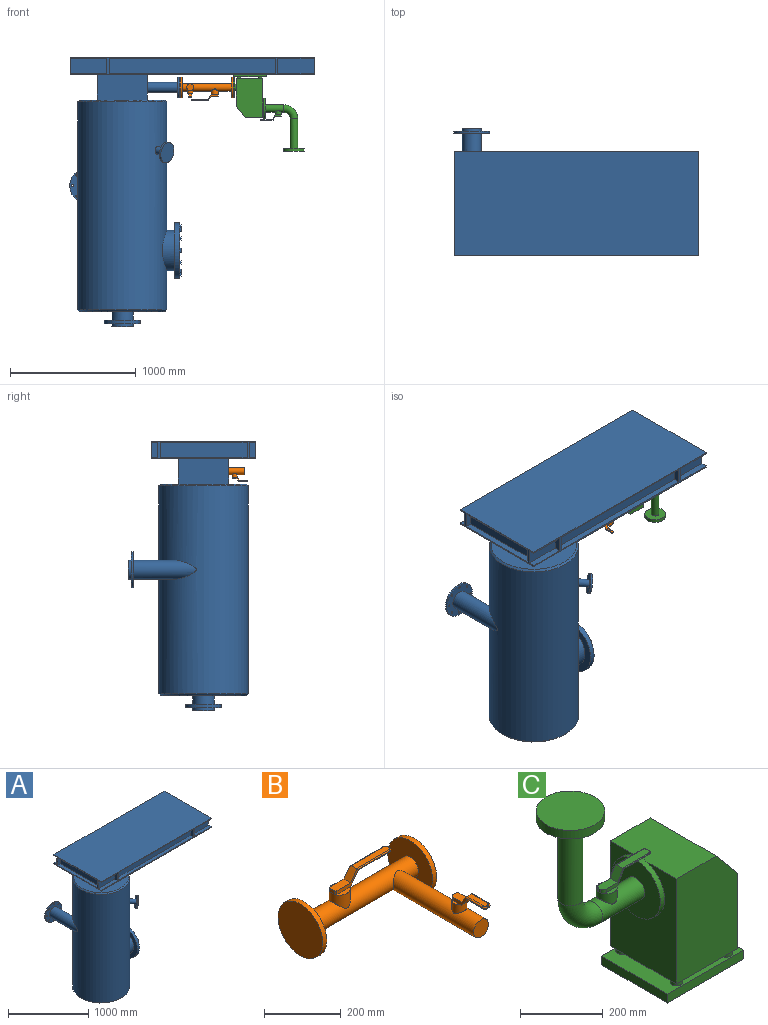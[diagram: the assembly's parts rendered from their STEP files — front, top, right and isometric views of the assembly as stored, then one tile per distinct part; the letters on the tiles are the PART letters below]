
ASSEMBLY  parts=3 mates=3
PART A: 183 faces, bbox 1942.5x1015x2142 mm
  f0: plane 830x140mm, normal (-1,0,0), area 21400mm2, adj f2,f3,f129,f130,f144,f146,f147,f153
  f1: plane 830x140mm, normal (1,0,0), area 21400mm2, adj f2,f3,f129,f130,f140,f141,f143,f157
  f2: plane 1940x140mm, normal (0,-1,0), area 43600mm2, adj f0,f1,f129,f130,f148,f149,f150,f151
  f3: plane 1940x140mm, normal (0,1,0), area 43600mm2, adj f0,f1,f129,f130,f135,f136,f137,f138
  f4: cylinder r=355mm len=1652mm, axis (0,0,-1), area 3567773.8mm2, adj f7,f10,f24,f111,f131
  f5: cylinder r=85mm len=170mm, axis (0,0,1), area 37385mm2, adj f9,f113
  f6: plane 445x445mm, normal (1,0,0), area 146689.4mm2, adj f25,f27,f28,f29,f30,f31,f32,f34
  f7: cylinder r=75mm len=500.65mm, axis (0,-1,0), area 167787.6mm2, adj f4,f13
  f8: plane 680x680mm, normal (0,0,1), area 203168.1mm2, adj f10,f125,f126,f127,f128
  f9: plane 680x680mm, normal (0,0,-1), area 340470.1mm2, adj f5,f111
  f10: cone r=355mm half-angle=45deg, axis (0,0,-1), area 46317.1mm2, adj f4,f8
  f11: cylinder r=142.5mm len=285mm, axis (0,-1,0), area 13430.3mm2, adj f12,f13
  f12: plane 285x285mm, normal (0,1,0), area 44086.8mm2, adj f11,f15,f16,f17,f18,f19,f20,f21
  f13: plane 285x285mm, normal (0,-1,0), area 44086.8mm2, adj f7,f11,f16,f17,f18,f19,f20,f21
  f14: plane 150x150mm, normal (0,1,0), area 17671.5mm2, adj f15
  f15: cylinder r=75mm len=150mm, axis (0,-1,0), area 11781mm2, adj f12,f14
  f16: cylinder r=9mm len=18mm, axis (0,1,0), area 848.2mm2, adj f12,f13
  f17: cylinder r=9mm len=18mm, axis (0,1,0), area 848.2mm2, adj f12,f13
  f18: cylinder r=9mm len=18mm, axis (0,1,0), area 848.2mm2, adj f12,f13
  f19: cylinder r=9mm len=18mm, axis (0,1,0), area 848.2mm2, adj f12,f13
  f20: cylinder r=9mm len=18mm, axis (0,1,0), area 848.2mm2, adj f12,f13
  f21: cylinder r=9mm len=18mm, axis (0,1,0), area 848.2mm2, adj f12,f13
  f22: cylinder r=9mm len=18mm, axis (0,1,0), area 848.2mm2, adj f12,f13
  f23: cylinder r=9mm len=18mm, axis (0,1,0), area 848.2mm2, adj f12,f13
  f24: cylinder r=160mm len=320mm, axis (-1,0,0), area 79181.6mm2, adj f4,f26
  f25: cylinder r=222.5mm len=445mm, axis (-1,0,0), area 55920.3mm2, adj f6,f26
  f26: plane 445x445mm, normal (-1,0,0), area 75103.7mm2, adj f24,f25
  f27: plane 15x14.58mm, normal (0,-0.87,0.5), area 252.6mm2, adj f6,f28,f32,f33
  f28: plane 15x14.58mm, normal (0,-0.87,-0.5), area 252.6mm2, adj f6,f27,f29,f33
  f29: plane 16.84x15mm, normal (0,0,-1), area 252.6mm2, adj f6,f28,f30,f33
  f30: plane 15x14.58mm, normal (0,0.87,-0.5), area 252.6mm2, adj f6,f29,f31,f33
  f31: plane 15x14.58mm, normal (0,0.87,0.5), area 252.6mm2, adj f6,f30,f32,f33
  f32: plane 16.84x15mm, normal (0,0,1), area 252.6mm2, adj f6,f27,f31,f33
  f33: plane 33.68x29.16mm, normal (1,0,0), area 736.6mm2, adj f27,f28,f29,f30,f31,f32
  f34: plane 15x14.58mm, normal (0,-0.5,-0.87), area 252.6mm2, adj f6,f35,f39,f40
  f35: plane 15x14.58mm, normal (0,0.5,-0.87), area 252.6mm2, adj f6,f34,f36,f40
  f36: plane 16.84x15mm, normal (0,1,0), area 252.6mm2, adj f6,f35,f37,f40
  f37: plane 15x14.58mm, normal (0,0.5,0.87), area 252.6mm2, adj f6,f36,f38,f40
  f38: plane 15x14.58mm, normal (0,-0.5,0.87), area 252.6mm2, adj f6,f37,f39,f40
  f39: plane 16.84x15mm, normal (0,-1,0), area 252.6mm2, adj f6,f34,f38,f40
  f40: plane 33.68x29.16mm, normal (1,0,0), area 736.6mm2, adj f34,f35,f36,f37,f38,f39
  f41: plane 16.84x15mm, normal (0,0,-1), area 252.6mm2, adj f6,f42,f46,f47
  f42: plane 15x14.58mm, normal (0,0.87,-0.5), area 252.6mm2, adj f6,f41,f43,f47
  f43: plane 15x14.58mm, normal (0,0.87,0.5), area 252.6mm2, adj f6,f42,f44,f47
  f44: plane 16.84x15mm, normal (0,0,1), area 252.6mm2, adj f6,f43,f45,f47
  f45: plane 15x14.58mm, normal (0,-0.87,0.5), area 252.6mm2, adj f6,f44,f46,f47
  f46: plane 15x14.58mm, normal (0,-0.87,-0.5), area 252.6mm2, adj f6,f41,f45,f47
  f47: plane 33.68x29.16mm, normal (1,0,0), area 736.6mm2, adj f41,f42,f43,f44,f45,f46
  f48: plane 15x14.58mm, normal (0,0.5,-0.87), area 252.6mm2, adj f6,f49,f53,f54
  f49: plane 16.84x15mm, normal (0,1,0), area 252.6mm2, adj f6,f48,f50,f54
  f50: plane 15x14.58mm, normal (0,0.5,0.87), area 252.6mm2, adj f6,f49,f51,f54
  f51: plane 15x14.58mm, normal (0,-0.5,0.87), area 252.6mm2, adj f6,f50,f52,f54
  f52: plane 16.84x15mm, normal (0,-1,0), area 252.6mm2, adj f6,f51,f53,f54
  f53: plane 15x14.58mm, normal (0,-0.5,-0.87), area 252.6mm2, adj f6,f48,f52,f54
  f54: plane 33.68x29.16mm, normal (1,0,0), area 736.6mm2, adj f48,f49,f50,f51,f52,f53
  f55: plane 15x14.58mm, normal (0,0.87,-0.5), area 252.6mm2, adj f6,f56,f60,f61
  f56: plane 15x14.58mm, normal (0,0.87,0.5), area 252.6mm2, adj f6,f55,f57,f61
  f57: plane 16.84x15mm, normal (0,0,1), area 252.6mm2, adj f6,f56,f58,f61
  f58: plane 15x14.58mm, normal (0,-0.87,0.5), area 252.6mm2, adj f6,f57,f59,f61
  f59: plane 15x14.58mm, normal (0,-0.87,-0.5), area 252.6mm2, adj f6,f58,f60,f61
  f60: plane 16.84x15mm, normal (0,0,-1), area 252.6mm2, adj f6,f55,f59,f61
  f61: plane 33.68x29.16mm, normal (1,0,0), area 736.6mm2, adj f55,f56,f57,f58,f59,f60
  f62: plane 16.84x15mm, normal (0,1,0), area 252.6mm2, adj f6,f63,f67,f68
  f63: plane 15x14.58mm, normal (0,0.5,0.87), area 252.6mm2, adj f6,f62,f64,f68
  f64: plane 15x14.58mm, normal (0,-0.5,0.87), area 252.6mm2, adj f6,f63,f65,f68
  f65: plane 16.84x15mm, normal (0,-1,0), area 252.6mm2, adj f6,f64,f66,f68
  f66: plane 15x14.58mm, normal (0,-0.5,-0.87), area 252.6mm2, adj f6,f65,f67,f68
  f67: plane 15x14.58mm, normal (0,0.5,-0.87), area 252.6mm2, adj f6,f62,f66,f68
  f68: plane 33.68x29.16mm, normal (1,0,0), area 736.6mm2, adj f62,f63,f64,f65,f66,f67
  f69: plane 15x14.58mm, normal (0,0.87,0.5), area 252.6mm2, adj f6,f70,f74,f75
  f70: plane 16.84x15mm, normal (0,0,1), area 252.6mm2, adj f6,f69,f71,f75
  f71: plane 15x14.58mm, normal (0,-0.87,0.5), area 252.6mm2, adj f6,f70,f72,f75
  f72: plane 15x14.58mm, normal (0,-0.87,-0.5), area 252.6mm2, adj f6,f71,f73,f75
  f73: plane 16.84x15mm, normal (0,0,-1), area 252.6mm2, adj f6,f72,f74,f75
  f74: plane 15x14.58mm, normal (0,0.87,-0.5), area 252.6mm2, adj f6,f69,f73,f75
  f75: plane 33.68x29.16mm, normal (1,0,0), area 736.6mm2, adj f69,f70,f71,f72,f73,f74
  f76: plane 15x14.58mm, normal (0,0.5,0.87), area 252.6mm2, adj f6,f77,f81,f82
  f77: plane 15x14.58mm, normal (0,-0.5,0.87), area 252.6mm2, adj f6,f76,f78,f82
  f78: plane 16.84x15mm, normal (0,-1,0), area 252.6mm2, adj f6,f77,f79,f82
  f79: plane 15x14.58mm, normal (0,-0.5,-0.87), area 252.6mm2, adj f6,f78,f80,f82
  f80: plane 15x14.58mm, normal (0,0.5,-0.87), area 252.6mm2, adj f6,f79,f81,f82
  f81: plane 16.84x15mm, normal (0,1,0), area 252.6mm2, adj f6,f76,f80,f82
  f82: plane 33.68x29.16mm, normal (1,0,0), area 736.6mm2, adj f76,f77,f78,f79,f80,f81
  f83: plane 16.84x15mm, normal (0,0,1), area 252.6mm2, adj f6,f84,f88,f89
  f84: plane 15x14.58mm, normal (0,-0.87,0.5), area 252.6mm2, adj f6,f83,f85,f89
  f85: plane 15x14.58mm, normal (0,-0.87,-0.5), area 252.6mm2, adj f6,f84,f86,f89
  f86: plane 16.84x15mm, normal (0,0,-1), area 252.6mm2, adj f6,f85,f87,f89
  f87: plane 15x14.58mm, normal (0,0.87,-0.5), area 252.6mm2, adj f6,f86,f88,f89
  f88: plane 15x14.58mm, normal (0,0.87,0.5), area 252.6mm2, adj f6,f83,f87,f89
  f89: plane 33.68x29.16mm, normal (1,0,0), area 736.6mm2, adj f83,f84,f85,f86,f87,f88
  f90: plane 15x14.58mm, normal (0,-0.5,0.87), area 252.6mm2, adj f6,f91,f95,f96
  f91: plane 16.84x15mm, normal (0,-1,0), area 252.6mm2, adj f6,f90,f92,f96
  f92: plane 15x14.58mm, normal (0,-0.5,-0.87), area 252.6mm2, adj f6,f91,f93,f96
  f93: plane 15x14.58mm, normal (0,0.5,-0.87), area 252.6mm2, adj f6,f92,f94,f96
  f94: plane 16.84x15mm, normal (0,1,0), area 252.6mm2, adj f6,f93,f95,f96
  f95: plane 15x14.58mm, normal (0,0.5,0.87), area 252.6mm2, adj f6,f90,f94,f96
  f96: plane 33.68x29.16mm, normal (1,0,0), area 736.6mm2, adj f90,f91,f92,f93,f94,f95
  f97: plane 15x14.58mm, normal (0,-0.87,0.5), area 252.6mm2, adj f6,f98,f102,f103
  f98: plane 15x14.58mm, normal (0,-0.87,-0.5), area 252.6mm2, adj f6,f97,f99,f103
  f99: plane 16.84x15mm, normal (0,0,-1), area 252.6mm2, adj f6,f98,f100,f103
  f100: plane 15x14.58mm, normal (0,0.87,-0.5), area 252.6mm2, adj f6,f99,f101,f103
  f101: plane 15x14.58mm, normal (0,0.87,0.5), area 252.6mm2, adj f6,f100,f102,f103
  f102: plane 16.84x15mm, normal (0,0,1), area 252.6mm2, adj f6,f97,f101,f103
  f103: plane 33.68x29.16mm, normal (1,0,0), area 736.6mm2, adj f97,f98,f99,f100,f101,f102
  f104: plane 16.84x15mm, normal (0,-1,0), area 252.6mm2, adj f6,f105,f109,f110
  f105: plane 15x14.58mm, normal (0,-0.5,-0.87), area 252.6mm2, adj f6,f104,f106,f110
  f106: plane 15x14.58mm, normal (0,0.5,-0.87), area 252.6mm2, adj f6,f105,f107,f110
  f107: plane 16.84x15mm, normal (0,1,0), area 252.6mm2, adj f6,f106,f108,f110
  f108: plane 15x14.58mm, normal (0,0.5,0.87), area 252.6mm2, adj f6,f107,f109,f110
  f109: plane 15x14.58mm, normal (0,-0.5,0.87), area 252.6mm2, adj f6,f104,f108,f110
  f110: plane 33.68x29.16mm, normal (1,0,0), area 736.6mm2, adj f104,f105,f106,f107,f108,f109
  f111: cone r=340mm half-angle=45deg, axis (0,0,1), area 46317.1mm2, adj f4,f9
  f112: cylinder r=142.5mm len=285mm, axis (0,0,-1), area 22383.8mm2, adj f113,f114
  f113: plane 285x285mm, normal (0,0,1), area 39060.2mm2, adj f5,f112,f117,f118,f119,f120,f121,f122
  f114: plane 285x285mm, normal (0,0,-1), area 39060.2mm2, adj f112,f116,f117,f118,f119,f120,f121,f122
  f115: plane 170x170mm, normal (0,0,-1), area 5026.5mm2, adj f116,f181
  f116: cylinder r=85mm len=170mm, axis (0,0,1), area 13351.8mm2, adj f114,f115
  f117: cylinder r=9mm len=25mm, axis (0,0,-1), area 1413.7mm2, adj f113,f114
  f118: cylinder r=9mm len=25mm, axis (0,0,-1), area 1413.7mm2, adj f113,f114
  f119: cylinder r=9mm len=25mm, axis (0,0,-1), area 1413.7mm2, adj f113,f114
  f120: cylinder r=9mm len=25mm, axis (0,0,-1), area 1413.7mm2, adj f113,f114
  f121: cylinder r=9mm len=25mm, axis (0,0,-1), area 1413.7mm2, adj f113,f114
  f122: cylinder r=9mm len=25mm, axis (0,0,-1), area 1413.7mm2, adj f113,f114
  f123: cylinder r=9mm len=25mm, axis (0,0,-1), area 1413.7mm2, adj f113,f114
  f124: cylinder r=9mm len=25mm, axis (0,0,-1), area 1413.7mm2, adj f113,f114
  f125: plane 400x200mm, normal (0,1,0), area 80000mm2, adj f8,f126,f128,f130
  f126: plane 400x200mm, normal (-1,0,0), area 80000mm2, adj f8,f125,f127,f130
  f127: plane 400x200mm, normal (0,-1,0), area 80000mm2, adj f8,f126,f128,f130
  f128: plane 400x200mm, normal (1,0,0), area 74973.5mm2, adj f8,f125,f127,f130,f171
  f129: plane 1940x830mm, normal (0,0,1), area 1610200mm2, adj f0,f1,f2,f3
  f130: plane 1940x830mm, normal (0,0,-1), area 1450200mm2, adj f0,f1,f2,f3,f125,f126,f127,f128
  f131: cylinder r=30mm len=108.08mm, axis (-0.78,0.61,0.17), area 16185.6mm2, adj f4,f134
  f132: cylinder r=82.5mm len=165.1mm, axis (-0.78,0.61,0.17), area 7775.4mm2, adj f133,f134
  f133: plane 162.49x131.21mm, normal (0.78,-0.61,-0.17), area 21382.5mm2, adj f132
  f134: plane 162.49x131.21mm, normal (-0.78,0.61,0.17), area 18555mm2, adj f131,f132
  f135: plane 120x50mm, normal (1,0,0), area 6000mm2, adj f3,f136,f138,f139
  f136: plane 1320x50mm, normal (0,0,-1), area 66000mm2, adj f3,f135,f137,f139
  f137: plane 120x50mm, normal (-1,0,0), area 6000mm2, adj f3,f136,f138,f139
  f138: plane 1320x50mm, normal (0,0,1), area 66000mm2, adj f3,f135,f137,f139
  f139: plane 1320x120mm, normal (0,1,0), area 158400mm2, adj f135,f136,f137,f138
  f140: plane 290x50mm, normal (0,0,-1), area 14500mm2, adj f1,f3,f142,f143
  f141: plane 290x50mm, normal (0,0,1), area 14500mm2, adj f1,f3,f142,f143
  f142: plane 120x50mm, normal (1,0,0), area 6000mm2, adj f3,f140,f141,f143
  f143: plane 290x120mm, normal (0,1,0), area 34800mm2, adj f1,f140,f141,f142
  f144: plane 290x50mm, normal (0,0,-1), area 14500mm2, adj f0,f3,f145,f147
  f145: plane 120x50mm, normal (-1,0,0), area 6000mm2, adj f3,f144,f146,f147
  f146: plane 290x50mm, normal (0,0,1), area 14500mm2, adj f0,f3,f145,f147
  f147: plane 290x120mm, normal (0,1,0), area 34800mm2, adj f0,f144,f145,f146
  f148: plane 1320x50mm, normal (0,0,1), area 66000mm2, adj f2,f149,f151,f152
  f149: plane 120x50mm, normal (-1,0,0), area 6000mm2, adj f2,f148,f150,f152
  f150: plane 1320x50mm, normal (0,0,-1), area 66000mm2, adj f2,f149,f151,f152
  f151: plane 120x50mm, normal (1,0,0), area 6000mm2, adj f2,f148,f150,f152
  f152: plane 1320x120mm, normal (0,-1,0), area 158400mm2, adj f148,f149,f150,f151
  f153: plane 290x50mm, normal (0,0,1), area 14500mm2, adj f0,f2,f154,f156
  f154: plane 120x50mm, normal (-1,0,0), area 6000mm2, adj f2,f153,f155,f156
  f155: plane 290x50mm, normal (0,0,-1), area 14500mm2, adj f0,f2,f154,f156
  f156: plane 290x120mm, normal (0,-1,0), area 34800mm2, adj f0,f153,f154,f155
  f157: plane 290x50mm, normal (0,0,1), area 14500mm2, adj f1,f2,f159,f160
  f158: plane 290x50mm, normal (0,0,-1), area 14500mm2, adj f1,f2,f159,f160
  f159: plane 120x50mm, normal (1,0,0), area 6000mm2, adj f2,f157,f158,f160
  f160: plane 290x120mm, normal (0,-1,0), area 34800mm2, adj f1,f157,f158,f159
  f161: plane 120x50mm, normal (0,-1,0), area 6000mm2, adj f1,f162,f164,f165
  f162: plane 690x50mm, normal (0,0,-1), area 34500mm2, adj f1,f161,f163,f165
  f163: plane 120x50mm, normal (0,1,0), area 6000mm2, adj f1,f162,f164,f165
  f164: plane 690x50mm, normal (0,0,1), area 34500mm2, adj f1,f161,f163,f165
  f165: plane 690x120mm, normal (1,0,0), area 82800mm2, adj f161,f162,f163,f164
  f166: plane 690x50mm, normal (0,0,1), area 34500mm2, adj f0,f167,f169,f170
  f167: plane 120x50mm, normal (0,1,0), area 6000mm2, adj f0,f166,f168,f170
  f168: plane 690x50mm, normal (0,0,-1), area 34500mm2, adj f0,f167,f169,f170
  f169: plane 120x50mm, normal (0,-1,0), area 6000mm2, adj f0,f166,f168,f170
  f170: plane 690x120mm, normal (-1,0,0), area 82800mm2, adj f166,f167,f168,f169
  f171: cylinder r=40mm len=240mm, axis (-1,0,0), area 60318.6mm2, adj f128,f174
  f172: cylinder r=82.5mm len=165mm, axis (-1,0,0), area 7775.4mm2, adj f173,f174
  f173: plane 165x165mm, normal (1,0,0), area 18401.1mm2, adj f172,f175,f176,f177,f178,f179
  f174: plane 165x165mm, normal (-1,0,0), area 15338mm2, adj f171,f172,f175,f176,f177,f178
  f175: cylinder r=9mm len=18mm, axis (1,0,0), area 848.2mm2, adj f173,f174
  f176: cylinder r=9mm len=18mm, axis (1,0,0), area 848.2mm2, adj f173,f174
  f177: cylinder r=9mm len=18mm, axis (1,0,0), area 848.2mm2, adj f173,f174
  f178: cylinder r=9mm len=18mm, axis (1,0,0), area 848.2mm2, adj f173,f174
  f179: cylinder r=25mm len=500mm, axis (1,0,0), area 78539.8mm2, adj f173,f180
  f180: plane 50x50mm, normal (1,0,0), area 1963.5mm2, adj f179
  f181: cylinder r=75mm len=1000mm, axis (0,0,-1), area 471238.9mm2, adj f115,f182
  f182: plane 150x150mm, normal (0,0,-1), area 17671.5mm2, adj f181
PART B: 68 faces, bbox 425x435.8x184.4 mm
  f0: plane 33.9x11.91mm, normal (0,0,1), area 168.6mm2, adj f39,f53,f66
  f1: cylinder r=27.5mm len=320.83mm, axis (0,1,0), area 51231mm2, adj f2,f38,f39
  f2: cylinder r=30mm len=390mm, axis (-1,0,0), area 67910.8mm2, adj f1,f5,f9,f12
  f3: plane 49.26x15.54mm, normal (0,0,1), area 525.2mm2, adj f12,f25,f36
  f4: cylinder r=82.5mm len=165mm, axis (-1,0,0), area 7775.4mm2, adj f5,f6
  f5: plane 165x165mm, normal (1,0,0), area 18555mm2, adj f2,f4
  f6: plane 165x165mm, normal (-1,0,0), area 21382.5mm2, adj f4
  f7: cylinder r=82.5mm len=165mm, axis (-1,0,0), area 7775.4mm2, adj f8,f9
  f8: plane 165x165mm, normal (1,0,0), area 3711mm2, adj f7,f10
  f9: plane 165x165mm, normal (-1,0,0), area 18555mm2, adj f2,f7
  f10: cylinder r=75mm len=150mm, axis (-1,0,0), area 2356.2mm2, adj f8,f11
  f11: plane 150x150mm, normal (1,0,0), area 17671.5mm2, adj f10
  f12: cylinder r=27.5mm len=55mm, axis (0,0,-1), area 6217mm2, adj f2,f3,f13,f14,f15,f16,f17
  f13: plane 49.26x15.54mm, normal (0,0,1), area 525.2mm2, adj f12,f24,f37
  f14: plane 11.96x2.74mm, normal (0,0,-1), area 7.2mm2, adj f12,f23,f36
  f15: plane 11.96x2.74mm, normal (0,0,-1), area 7.2mm2, adj f12,f23,f37
  f16: plane 12.5x3.01mm, normal (0,0,-1), area 12.2mm2, adj f12,f18,f25
  f17: plane 12.5x3.01mm, normal (0,0,-1), area 12.2mm2, adj f12,f18,f24
  f18: plane 40.95x29.69mm, normal (0.81,0,-0.59), area 1123.4mm2, adj f16,f17,f19,f24,f25,f31,f35
  f19: plane 123x15mm, normal (0,0,-1), area 1834.3mm2, adj f18,f31,f32,f33,f34,f35
  f20: plane 127x19mm, normal (0,0,1), area 2392mm2, adj f21,f26,f27,f28,f29,f30
  f21: plane 31.95x25mm, normal (-0.8,0,0.6), area 995.2mm2, adj f20,f22,f24,f25,f26,f30
  f22: plane 55x25mm, normal (0,0,1), area 1364.3mm2, adj f21,f23,f24,f25,f36,f37
  f23: plane 15x12mm, normal (-1,0,0), area 180mm2, adj f14,f15,f22,f36,f37
  f24: plane 79.69x40.95mm, normal (0,-1,0), area 892.3mm2, adj f13,f17,f18,f21,f22,f26,f37
  f25: plane 79.69x40.95mm, normal (0,1,0), area 892.3mm2, adj f3,f16,f18,f21,f22,f30,f36
  f26: cylinder r=3mm len=122.26mm, axis (1,0,0), area 569.4mm2, adj f20,f21,f24,f27,f31
  f27: torus R=7mm, axis (0,0,1), area 66mm2, adj f20,f26,f28,f32
  f28: cylinder r=3mm len=5mm, axis (0,1,0), area 23.6mm2, adj f20,f27,f29,f33
  f29: torus R=7mm, axis (0,0,1), area 66mm2, adj f20,f28,f30,f34
  f30: cylinder r=3mm len=122.26mm, axis (-1,0,0), area 569.4mm2, adj f20,f21,f25,f29,f35
  f31: cylinder r=5mm len=118mm, axis (-1,0,0), area 916.4mm2, adj f18,f19,f26,f32
  f32: torus R=5mm, axis (0,0,-1), area 101mm2, adj f19,f27,f31,f33
  f33: cylinder r=5mm len=5mm, axis (0,1,0), area 39.3mm2, adj f19,f28,f32,f34
  f34: torus R=5mm, axis (0,0,-1), area 101mm2, adj f19,f29,f33,f35
  f35: cylinder r=5mm len=118mm, axis (1,0,0), area 916.4mm2, adj f18,f19,f30,f34
  f36: cylinder r=5mm len=12mm, axis (0,0,-1), area 94.2mm2, adj f3,f14,f22,f23,f25
  f37: cylinder r=5mm len=12mm, axis (0,0,1), area 94.2mm2, adj f13,f15,f22,f23,f24
  f38: plane 55x55mm, normal (0,-1,0), area 2375.8mm2, adj f1
  f39: cylinder r=20mm len=40mm, axis (0,0,-1), area 3344.2mm2, adj f0,f1,f40,f41,f42,f43,f44
  f40: plane 33.9x11.91mm, normal (0,0,1), area 168.6mm2, adj f39,f52,f67
  f41: plane 8.09x1.71mm, normal (0,0,-1), area 1.5mm2, adj f39,f47,f67
  f42: plane 8.09x1.71mm, normal (0,0,-1), area 1.5mm2, adj f39,f47,f66
  f43: plane 12.5x4.39mm, normal (0,0,-1), area 17.4mm2, adj f39,f46,f53
  f44: plane 12.5x4.39mm, normal (0,0,-1), area 17.4mm2, adj f39,f46,f52
  f45: plane 63.15x15mm, normal (0,0,-1), area 936.5mm2, adj f46,f61,f62,f63,f64,f65
  f46: plane 30.28x25mm, normal (0,-0.81,-0.59), area 794.1mm2, adj f43,f44,f45,f52,f53,f61,f65
  f47: plane 10x5mm, normal (0,1,0), area 50mm2, adj f41,f42,f48,f66,f67
  f48: plane 40x25mm, normal (0,0,1), area 957.1mm2, adj f47,f49,f52,f53,f66,f67
  f49: plane 25x24.52mm, normal (0,0.83,0.56), area 730.6mm2, adj f48,f50,f52,f53,f56,f60
  f50: plane 66x17mm, normal (0,0,1), area 1106.5mm2, adj f49,f56,f57,f58,f59,f60
  f51: plane 5x0.25mm, normal (0,-1,0), area 1.2mm2, adj f54,f55,f58,f63
  f52: plane 106.5x30.52mm, normal (1,0,0), area 509.8mm2, adj f40,f44,f46,f48,f49,f55,f56,f61
  f53: plane 106.5x30.52mm, normal (-1,0,0), area 509.8mm2, adj f0,f43,f46,f48,f49,f54,f60,f65
  f54: cylinder r=10mm len=10mm, axis (0,0,-1), area 3.9mm2, adj f51,f53,f59,f64
  f55: cylinder r=10mm len=10mm, axis (0,0,1), area 3.9mm2, adj f51,f52,f57,f62
  f56: cylinder r=4mm len=62.69mm, axis (0,1,0), area 383.1mm2, adj f49,f50,f52,f57
  f57: torus R=6mm, axis (0,0,-1), area 84.4mm2, adj f50,f55,f56,f58
  f58: cylinder r=4mm len=5mm, axis (-1,0,0), area 31.4mm2, adj f50,f51,f57,f59
  f59: torus R=6mm, axis (0,0,-1), area 84.4mm2, adj f50,f54,f58,f60
  f60: cylinder r=4mm len=62.69mm, axis (0,-1,0), area 383.1mm2, adj f49,f50,f53,f59
  f61: cylinder r=5mm len=58.15mm, axis (0,-1,0), area 446.4mm2, adj f45,f46,f52,f62
  f62: torus R=5mm, axis (0,0,1), area 101mm2, adj f45,f55,f61,f63
  f63: cylinder r=5mm len=5mm, axis (-1,0,0), area 39.3mm2, adj f45,f51,f62,f64
  f64: torus R=5mm, axis (0,0,1), area 101mm2, adj f45,f54,f63,f65
  f65: cylinder r=5mm len=58.15mm, axis (0,1,0), area 446.4mm2, adj f45,f46,f53,f64
  f66: cylinder r=10mm len=10mm, axis (0,0,1), area 157.1mm2, adj f0,f42,f47,f48,f53
  f67: cylinder r=10mm len=10mm, axis (0,0,-1), area 157.1mm2, adj f40,f41,f47,f48,f52
PART C: 58 faces, bbox 566.5x225x621 mm
  f0: plane 45.75x18.36mm, normal (0,0,1), area 392.5mm2, adj f32,f45,f56
  f1: cylinder r=30mm len=144mm, axis (-1,0,0), area 24935.6mm2, adj f16,f28,f32
  f2: cylinder r=30mm len=235mm, axis (0,0,1), area 44296.5mm2, adj f28,f30
  f3: plane 225x136.03mm, normal (0,0,1), area 30605.7mm2, adj f4,f7,f8,f9
  f4: plane 310x225mm, normal (-1,0,0), area 66922.6mm2, adj f3,f5,f8,f9,f14
  f5: plane 225x210mm, normal (0,0,-1), area 44422.6mm2, adj f4,f6,f8,f9,f18,f19,f20,f21
  f6: plane 225x222.49mm, normal (1,0,0), area 47233.8mm2, adj f5,f7,f8,f9,f10
  f7: plane 225x87.51mm, normal (0.76,0,0.65), area 25781.4mm2, adj f3,f6,f8,f9
  f8: plane 310x210mm, normal (0,-1,0), area 61863.4mm2, adj f3,f4,f5,f6,f7
  f9: plane 310x210mm, normal (0,1,0), area 61863.4mm2, adj f3,f4,f5,f6,f7
  f10: cylinder r=30mm len=60mm, axis (-1,0,0), area 1885mm2, adj f6,f13
  f11: cylinder r=82.5mm len=165mm, axis (-1,0,0), area 7775.4mm2, adj f12,f13
  f12: plane 165x165mm, normal (1,0,0), area 21382.5mm2, adj f11
  f13: plane 165x165mm, normal (-1,0,0), area 18555mm2, adj f10,f11
  f14: cylinder r=30mm len=60mm, axis (1,0,0), area 1885mm2, adj f4,f17
  f15: cylinder r=82.5mm len=165mm, axis (1,0,0), area 7775.4mm2, adj f16,f17
  f16: plane 165x165mm, normal (-1,0,0), area 18555mm2, adj f1,f15
  f17: plane 165x165mm, normal (1,0,0), area 18555mm2, adj f14,f15
  f18: cylinder r=15mm len=30mm, axis (0,0,1), area 1413.7mm2, adj f5,f27
  f19: cylinder r=15mm len=30mm, axis (0,0,1), area 1413.7mm2, adj f5,f27
  f20: cylinder r=15mm len=30mm, axis (0,0,1), area 1413.7mm2, adj f5,f27
  f21: cylinder r=15mm len=30mm, axis (0,0,1), area 1413.7mm2, adj f5,f27
  f22: plane 225x26mm, normal (-1,0,0), area 5850mm2, adj f23,f25,f26,f27
  f23: plane 260x26mm, normal (0,1,0), area 6760mm2, adj f22,f24,f26,f27
  f24: plane 225x26mm, normal (1,0,0), area 5850mm2, adj f23,f25,f26,f27
  f25: plane 260x26mm, normal (0,-1,0), area 6760mm2, adj f22,f24,f26,f27
  f26: plane 260x225mm, normal (0,0,-1), area 58500mm2, adj f22,f23,f24,f25
  f27: plane 260x225mm, normal (0,0,1), area 55672.6mm2, adj f18,f19,f20,f21,f22,f23,f24,f25
  f28: torus R=80mm, axis (0,1,0), area 23687.1mm2, adj f1,f2
  f29: cylinder r=82.5mm len=165mm, axis (0,0,1), area 12959.1mm2, adj f30,f31
  f30: plane 165x165mm, normal (0,0,-1), area 18555mm2, adj f2,f29
  f31: plane 165x165mm, normal (0,0,1), area 21382.5mm2, adj f29
  f32: cylinder r=25mm len=50mm, axis (0,0,-1), area 4119.5mm2, adj f0,f1,f33,f34,f35,f36,f37
  f33: plane 45.75x18.36mm, normal (0,0,1), area 392.5mm2, adj f32,f44,f57
  f34: plane 6.64x0.9mm, normal (0,0,-1), area 0.8mm2, adj f32,f43,f56
  f35: plane 6.64x0.9mm, normal (0,0,-1), area 0.8mm2, adj f32,f43,f57
  f36: plane 12.5x3.35mm, normal (0,0,-1), area 13.6mm2, adj f32,f38,f45
  f37: plane 12.5x3.35mm, normal (0,0,-1), area 13.6mm2, adj f32,f38,f44
  f38: plane 40.04x25mm, normal (0.88,0,-0.47), area 1066.7mm2, adj f36,f37,f39,f44,f45,f51,f55
  f39: plane 93.03x16.2mm, normal (0,0,-1), area 1493.7mm2, adj f38,f51,f52,f53,f54,f55
  f40: plane 98x21mm, normal (0,0,1), area 2030.5mm2, adj f41,f46,f47,f48,f49,f50
  f41: plane 32.04x25mm, normal (-0.88,0,0.48), area 908.4mm2, adj f40,f42,f44,f45,f46,f50
  f42: plane 50x25mm, normal (0,0,1), area 1207.1mm2, adj f41,f43,f44,f45,f56,f57
  f43: plane 10x5mm, normal (-1,0,0), area 50mm2, adj f34,f35,f42,f56,f57
  f44: plane 61.28x40.04mm, normal (0,-1,0), area 582.2mm2, adj f33,f37,f38,f41,f42,f46,f57
  f45: plane 61.28x40.04mm, normal (0,1,0), area 582.2mm2, adj f0,f36,f38,f41,f42,f50,f56
  f46: cylinder r=2mm len=91.08mm, axis (1,0,0), area 284mm2, adj f40,f41,f44,f47,f51
  f47: torus R=8mm, axis (0,0,1), area 45.8mm2, adj f40,f46,f48,f52
  f48: cylinder r=2mm len=5mm, axis (0,1,0), area 15.7mm2, adj f40,f47,f49,f53
  f49: torus R=8mm, axis (0,0,1), area 45.8mm2, adj f40,f48,f50,f54
  f50: cylinder r=2mm len=91.08mm, axis (-1,0,0), area 284mm2, adj f40,f41,f45,f49,f55
  f51: cylinder r=5mm len=87.43mm, axis (1,0,0), area 467.7mm2, adj f38,f39,f46,f52
  f52: torus R=5.6mm, axis (0,0,1), area 67.9mm2, adj f39,f47,f51,f53
  f53: cylinder r=5mm len=5mm, axis (0,1,0), area 26.9mm2, adj f39,f48,f52,f54
  f54: torus R=5.6mm, axis (0,0,1), area 67.9mm2, adj f39,f49,f53,f55
  f55: cylinder r=5mm len=87.43mm, axis (1,0,0), area 467.7mm2, adj f38,f39,f50,f54
  f56: cylinder r=10mm len=10mm, axis (0,0,-1), area 157.1mm2, adj f0,f34,f42,f43,f45
  f57: cylinder r=10mm len=10mm, axis (0,0,1), area 157.1mm2, adj f33,f35,f42,f43,f44
PLACE A t=(-523.81,246.45,-508.5)mm fixed
PLACE B rot(axis=(0,1,0),180deg) t=(591.19,358.95,1345.55)mm
PLACE C rot(axis=(0,1,0),180deg) t=(591.19,358.95,1345.55)mm
MATE parallel C.f27 <-> A.f130  axis (0,0,-1) through (621.19,246.45,1360.55)mm
MATE revolute A.f171 <-> B.f4  axis (1,0,0) through (-68.81,246.45,1273.5)mm
MATE planar B.f4 <-> A.f179  axis (-1,0,0) through (-68.81,246.45,1273.5)mm
